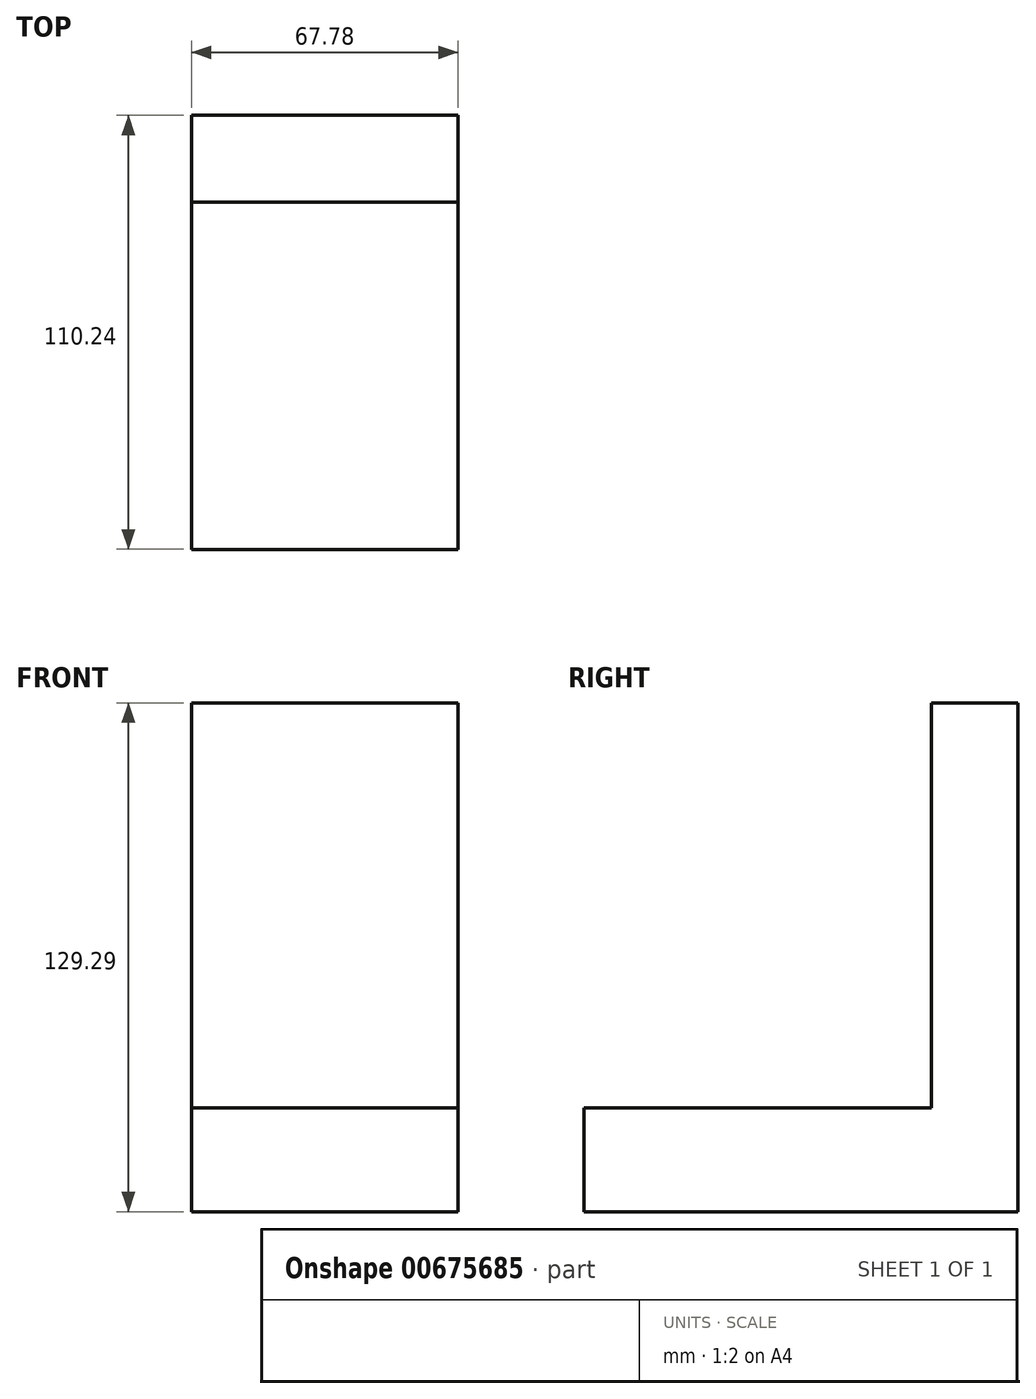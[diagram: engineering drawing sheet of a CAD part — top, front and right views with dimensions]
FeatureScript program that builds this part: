
annotation { "Feature Type Name" : "Feature", "Feature Type Description" : "" }
export const myFeature = defineFeature(function(context is Context, id is Id, definition is map)
    precondition{}
    {
        {
            var Q0;
            Q0=qCreatedBy(makeId("Top.planeOp"),FACE);
            var sketch = newSketch(context, id + "F0", { "sketchPlane" : qUnion([Q0])});
            skLineSegment(sketch, "E0.bottom", {"start": v(33.89, 55.12) * mm, "end": v(-33.89, 55.12) * mm});
            skLineSegment(sketch, "E0.top", {"start": v(33.89, -55.12) * mm, "end": v(-33.89, -55.12) * mm});
            skLineSegment(sketch, "E0.left", {"start": v(33.89, 55.12) * mm, "end": v(33.89, -55.12) * mm});
            skLineSegment(sketch, "E0.right", {"start": v(-33.89, 55.12) * mm, "end": v(-33.89, -55.12) * mm});
            skPoint(sketch, "E0.middle", {"position": v(0, 0) * mm});
            skSolve(sketch);
        }
        {
            var Q0;
            Q0=qSketchRegion(id+"F0",true);
            extrude(context, id + "F1", {"entities" : qUnion([Q0]), "depth" : 10.67 * mm, "offsetDistance" : 25.4 * mm});
        }
        {
            var Q0;
            Q0=makeQuery(id+"F1.opExtrude","CAP_FACE",FACE,{"disambiguationData":[OSD([sQuery(id+"F0.wireOp",EDGE,"E0.bottom"),sQuery(id+"F0.wireOp",EDGE,"E0.top"),sQuery(id+"F0.wireOp",EDGE,"E0.left"),sQuery(id+"F0.wireOp",EDGE,"E0.right")])],"isStart":false});
            var sketch = newSketch(context, id + "F2", { "sketchPlane" : qUnion([Q0])});
            skLineSegment(sketch, "E1.bottom", {"start": v(-33.89, 55.12) * mm, "end": v(33.89, 55.12) * mm});
            skLineSegment(sketch, "E1.top", {"start": v(-33.89, 33.14) * mm, "end": v(33.89, 33.14) * mm});
            skLineSegment(sketch, "E1.left", {"start": v(-33.89, 55.12) * mm, "end": v(-33.89, 33.14) * mm});
            skLineSegment(sketch, "E1.right", {"start": v(33.89, 55.12) * mm, "end": v(33.89, 33.14) * mm});
            skSolve(sketch);
        }
        {
            var Q0;
            Q0=makeQuery(id+"F2.imprint","IMPRINT",FACE,{"disambiguationData":[TD([[makeQuery(id+"F2.imprint","IMPRINT",EDGE,{"derivedFrom":sQuery(id+"F2.wireOp",EDGE,"E1.bottom")}),1.0]])]});
            extrude(context, id + "F3", {"entities" : qUnion([Q0]), "operationType" : NewBodyOperationType.ADD, "depth" : 84.07 * mm, "offsetDistance" : 25.4 * mm});
        }
        {
            var Q0;
            Q0=makeQuery(id+"F1.opExtrude","CAP_FACE",FACE,{"disambiguationData":[OSD([sQuery(id+"F0.wireOp",EDGE,"E0.bottom"),sQuery(id+"F0.wireOp",EDGE,"E0.top"),sQuery(id+"F0.wireOp",EDGE,"E0.left"),sQuery(id+"F0.wireOp",EDGE,"E0.right")])],"isStart":false});
            extrude(context, id + "F4", {"entities" : qUnion([Q0]), "operationType" : NewBodyOperationType.ADD, "depth" : 15.75 * mm, "offsetDistance" : 25.4 * mm});
        }
        {
            var Q0;
            Q0=makeQuery(id+"F3.opExtrude","CAP_FACE",FACE,{"disambiguationData":[OSD([sQuery(id+"F2.wireOp",EDGE,"E1.bottom"),sQuery(id+"F2.wireOp",EDGE,"E1.top"),sQuery(id+"F2.wireOp",EDGE,"E1.left"),sQuery(id+"F2.wireOp",EDGE,"E1.right")])],"isStart":false});
            extrude(context, id + "F5", {"entities" : qUnion([Q0]), "operationType" : NewBodyOperationType.ADD, "depth" : 34.54 * mm, "offsetDistance" : 25.4 * mm});
        }
    });
